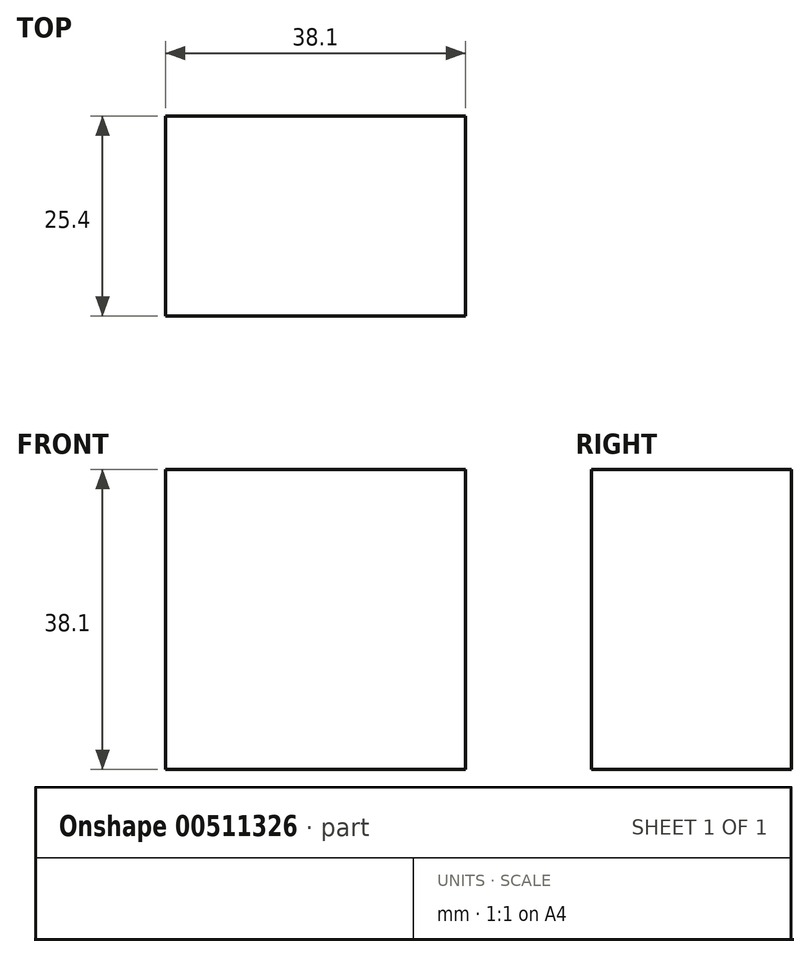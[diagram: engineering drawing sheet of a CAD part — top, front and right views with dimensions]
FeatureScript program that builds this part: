
annotation { "Feature Type Name" : "Feature", "Feature Type Description" : "" }
export const myFeature = defineFeature(function(context is Context, id is Id, definition is map)
    precondition{}
    {
        {
            var Q0;
            Q0=qCreatedBy(makeId("Front.planeOp"),FACE);
            var sketch = newSketch(context, id + "F0", { "sketchPlane" : qUnion([Q0])});
            skLineSegment(sketch, "E0", {"start": v(0, 0) * mm, "end": v(0, 38.1) * mm});
            skLineSegment(sketch, "E1", {"start": v(0, 38.1) * mm, "end": v(38.1, 38.1) * mm});
            skLineSegment(sketch, "E2", {"start": v(38.1, 38.1) * mm, "end": v(38.1, 0) * mm});
            skLineSegment(sketch, "E3", {"start": v(0, 0) * mm, "end": v(38.1, 0) * mm});
            skSolve(sketch);
        }
        {
            var Q0;
            Q0=makeQuery(id+"F0.imprint","IMPRINT",FACE,{"disambiguationData":[TD([[makeQuery(id+"F0.imprint","IMPRINT",EDGE,{"derivedFrom":sQuery(id+"F0.wireOp",EDGE,"E0")}),-1.0]])]});
            extrude(context, id + "F1", {"entities" : qUnion([Q0]), "depth" : 25.4 * mm, "offsetDistance" : 25.4 * mm});
        }
    });
